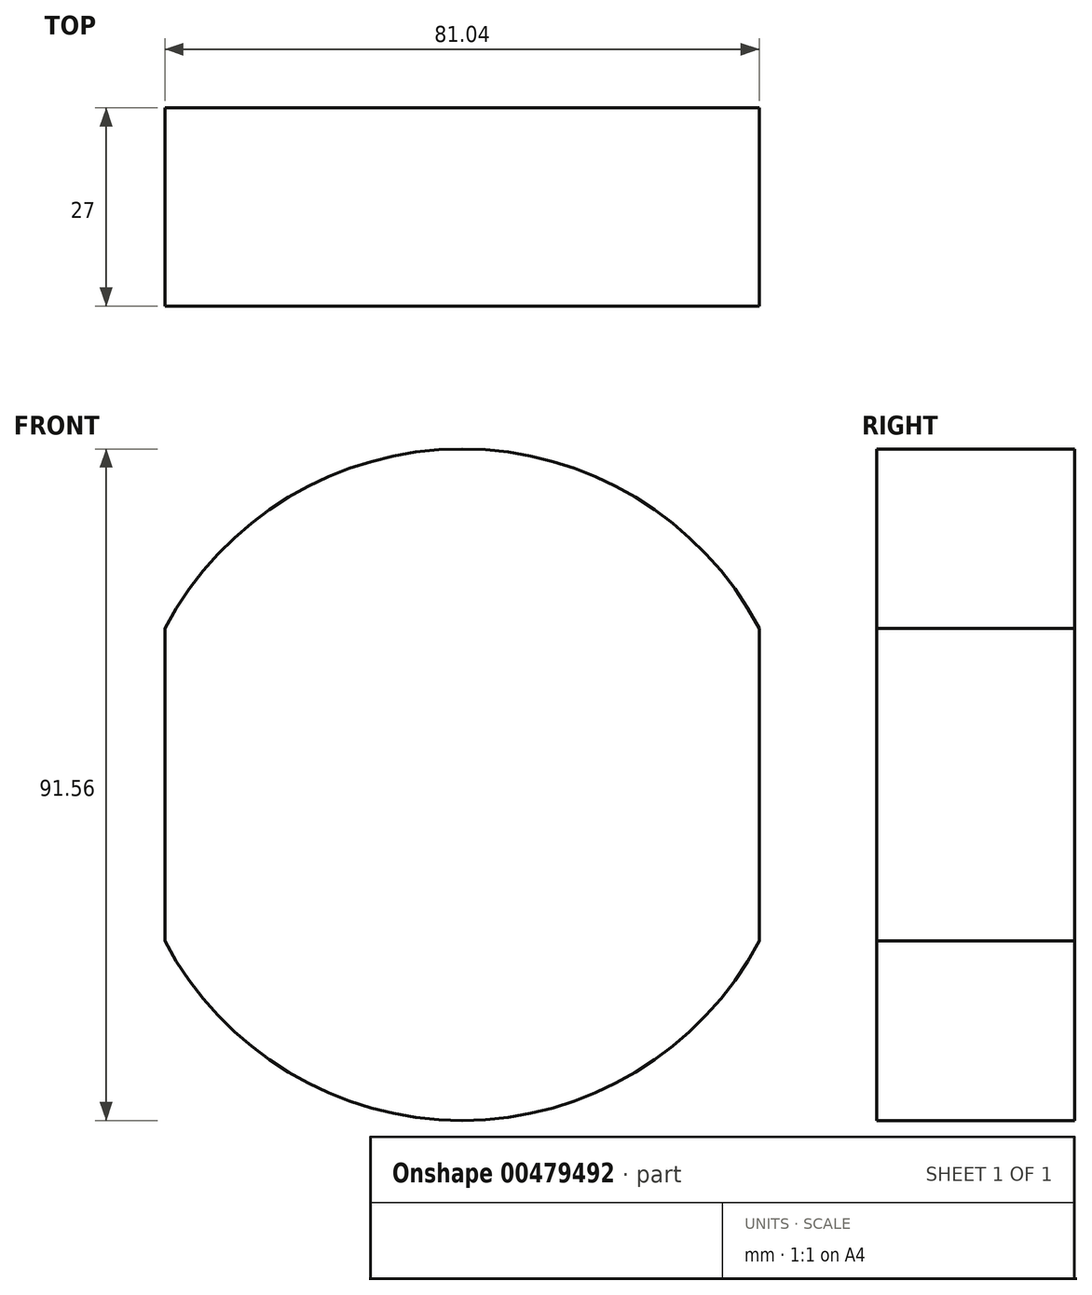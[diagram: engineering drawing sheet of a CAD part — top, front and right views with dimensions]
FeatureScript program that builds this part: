
annotation { "Feature Type Name" : "Feature", "Feature Type Description" : "" }
export const myFeature = defineFeature(function(context is Context, id is Id, definition is map)
    precondition{}
    {
        {
            var Q0;
            Q0=qCreatedBy(makeId("Front.planeOp"),FACE);
            var sketch = newSketch(context, id + "F0", { "sketchPlane" : qUnion([Q0])});
            skArc(sketch, "E0", {"start": v(-40.52, -21.31) * mm, "mid": v(0, -45.78) * mm, "end": v(40.52, -21.31) * mm});
            skLineSegment(sketch, "E1", {"start": v(-40.52, 21.31) * mm, "end": v(-40.52, -21.31) * mm});
            skLineSegment(sketch, "E2.MirrorCS", {"start": v(40.52, 21.31) * mm, "end": v(40.52, -21.31) * mm});
            skArc(sketch, "E3.trimOffspring", {"start": v(40.52, 21.31) * mm, "mid": v(0, 45.78) * mm, "end": v(-40.52, 21.31) * mm});
            skSolve(sketch);
        }
        {
            var Q0;
            Q0=makeQuery(id+"F0.imprint","IMPRINT",FACE,{"disambiguationData":[TD([[makeQuery(id+"F0.imprint","IMPRINT",EDGE,{"derivedFrom":sQuery(id+"F0.wireOp",EDGE,"E0")}),1.0]])]});
            extrude(context, id + "F1", {"entities" : qUnion([Q0]), "depth" : 27 * mm});
        }
    });
